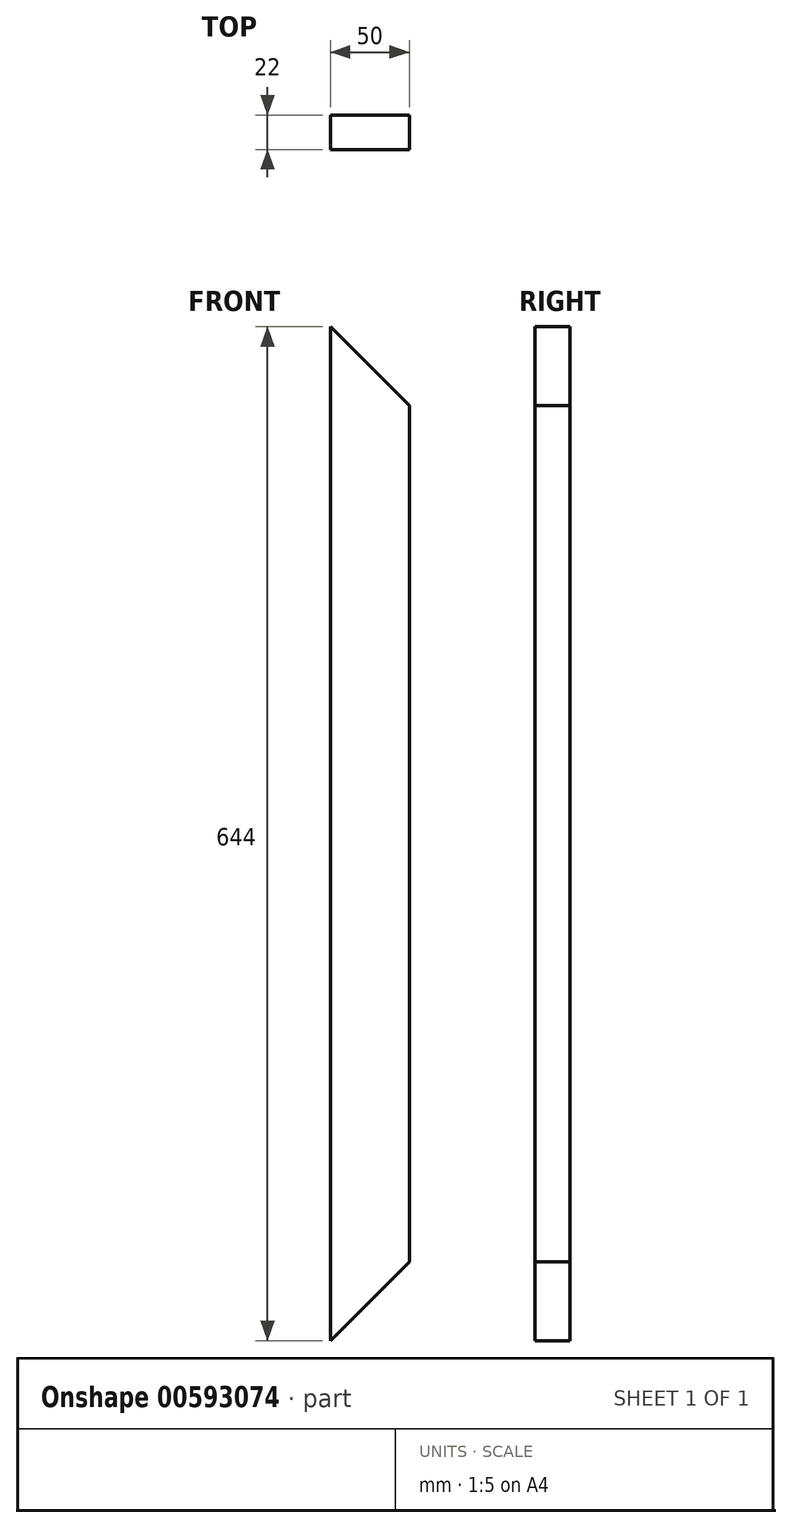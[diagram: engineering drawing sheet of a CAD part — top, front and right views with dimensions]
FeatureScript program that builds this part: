
annotation { "Feature Type Name" : "Feature", "Feature Type Description" : "" }
export const myFeature = defineFeature(function(context is Context, id is Id, definition is map)
    precondition{}
    {
        {
            var Q0;
            Q0=qCreatedBy(makeId("Front.planeOp"),FACE);
            var sketch = newSketch(context, id + "F0", { "sketchPlane" : qUnion([Q0])});
            skLineSegment(sketch, "E0.left", {"start": v(-50, 322) * mm, "end": v(-50, -322) * mm});
            skLineSegment(sketch, "E0.right", {"start": v(0, 272) * mm, "end": v(0, -272) * mm});
            skLineSegment(sketch, "E1", {"start": v(-50, 322) * mm, "end": v(0, 272) * mm});
            skLineSegment(sketch, "E2", {"start": v(-50, -322) * mm, "end": v(0, -272) * mm});
            skSolve(sketch);
        }
        {
            var Q0;
            Q0=makeQuery(id+"F0.imprint","IMPRINT",FACE,{"disambiguationData":[TD([[makeQuery(id+"F0.imprint","IMPRINT",EDGE,{"derivedFrom":sQuery(id+"F0.wireOp",EDGE,"E0.left")}),1.0]])]});
            extrude(context, id + "F1", {"entities" : qUnion([Q0]), "depth" : 22 * mm, "offsetDistance" : 25 * mm});
        }
    });
